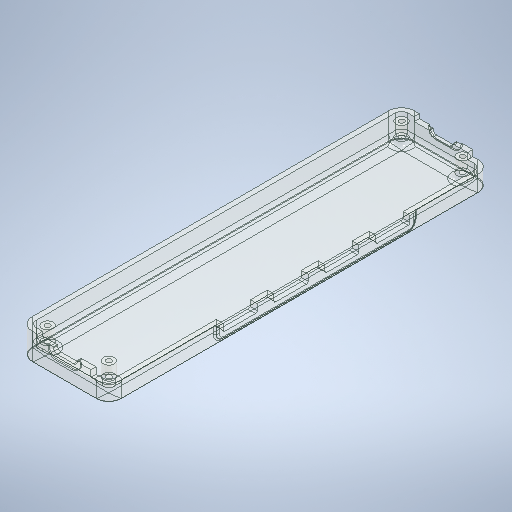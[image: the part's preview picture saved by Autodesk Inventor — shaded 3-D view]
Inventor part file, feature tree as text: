
AUTODESK INVENTOR PART (.ipt)
format: ipt  version: 2025.1 (Build 291241020, 241B)  size: 674,304 bytes
history: native  units: mm
features: extrude x14, sketch x7, other x4, thread x4, fillet x3, chamfer x2
ambient origin geometry x8: Origin, YZ Plane, XZ Plane, XY Plane, X Axis, Y Axis, Z Axis, Center Point
bodies: Body1 (feature_tree)
feature tree (34):
  other  "Sólido1"
  sketch  "Esboço1"  dims[d4=146.0mm d5=31.0mm]
  extrude  "Extrusão1"  Depth=31.0mm
  extrude  "Extrusão2"  Depth=145.0mm
  extrude  "Extrusão3"  Depth=3.0mm
  extrude  "Extrusão5"  Depth=3.0mm
  extrude  "Extrusão6"  Depth=2.0mm
  extrude  "Extrusão7"  Depth=5.0mm
  extrude  "Extrusão8"  Depth=0.52mm TaperAngle=0.0deg
  extrude  "Extrusão9"  Depth=0.52mm
  extrude  "Extrusão10"  Depth=0.52mm TaperAngle=0.0deg
  extrude  "Extrusão11"  Depth=0.52mm
  extrude  "Extrusão12"  Depth=0.52mm
  thread  "Rosca1"  [1 undecoded]
  thread  "Rosca2"  [1 undecoded]
  thread  "Rosca3"  [1 undecoded]
  thread  "Rosca4"  [1 undecoded]
  fillet  "Arredondamento1"  Radius=2.5mm
  extrude  "Extrusão13"  Depth=0.52mm
  chamfer  "Chanfro2"  Distance=13.4mm
  fillet  "Arredondamento4"  Radius=6.6mm
  chamfer  "Chanfro3"  Distance=6.6mm
  fillet  "Arredondamento5"  Radius=6.6mm
  extrude  "Extrusão14"  Depth=0.52mm
  extrude  "Extrusão15"  Depth=0.52mm
  sketch  "Esboço2"  dims[d7=30.0mm d8=145.0mm]
  sketch  "Esboço3"  dims[d9=3.0mm d10=3.0mm]
  sketch  "Esboço4"  dims[d11=3.0mm d12=3.0mm]
  sketch  "Esboço6"  dims[d13=2.0mm d14=2.0mm]
  other  "Contorno projetado1"
  sketch  "Esboço10"  dims[d15=2.5mm d16=5.0mm]
  other  "Contorno projetado2"
  sketch  "Esboço11"  dims[d17=3.0mm d18=0.0mm d19=10.463mm d20=0.0mm d21=4.3mm d22=3.0mm d23=0.0mm d24=7.0mm d25=7.0mm d28=7.0mm d29=7.0mm d30=6.86mm d31=0.0mm d32=2.5mm d33=2.5mm d34=3.835mm d35=13.4mm d36=6.6mm d37=6.6mm d38=6.6mm d39=32.37mm d40=44.23mm d41=0.65mm d42=6.86mm d43=0.0mm d44=9.35mm d45=0.0mm d46=9.24mm d47=7.525mm d48=12.892mm d49=12.868mm d50=1.45mm d51=9.35mm d52=0.0mm d53=9.275mm d54=0.0mm d55=9.24mm d56=7.635mm d57=12.88mm d58=12.88mm d59=1.45mm d60=9.275mm d61=0.0mm d62=10.963mm d63=0.0mm d64=5.0mm d65=0.0mm d69=5.463mm d70=0.0mm d71=5.463mm d72=0.0mm d73=5.463mm d74=0.0mm d75=5.463mm d76=0.0mm d77=2.0mm d80=2.0mm d81=2.0mm d82=2.0mm d83=2.325mm d84=0.65mm d85=0.0mm d86=0.65mm d87=2.0mm d88=45.0deg d89=1.0mm d93=5.0mm d94=0.5mm d95=45.0deg d96=0.2mm d97=1.75mm d98=1.75mm d99=1.75mm d100=3.2mm d101=0.52mm d102=0.0mm d103=1.75mm d104=1.75mm d105=1.75mm d106=3.2mm d107=0.52mm d108=0.0mm]
  other  "Contorno projetado3"
note: 4 required parameter values undecoded (feature->parameter linkage not recoverable at this tier; creation-order binding heuristic only, values carry confidence <= 0.55)
